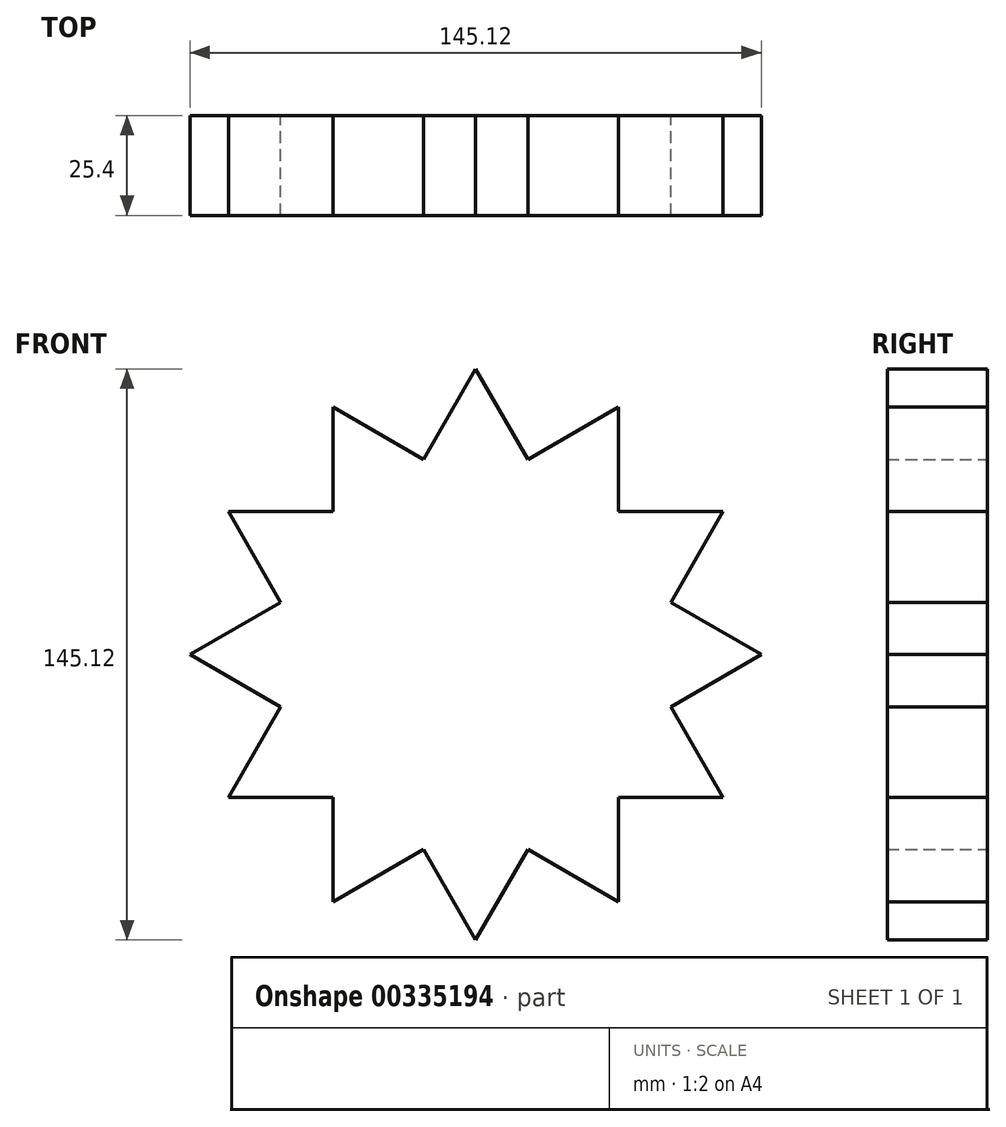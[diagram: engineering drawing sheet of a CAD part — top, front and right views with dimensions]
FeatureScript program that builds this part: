
annotation { "Feature Type Name" : "Feature", "Feature Type Description" : "" }
export const myFeature = defineFeature(function(context is Context, id is Id, definition is map)
    precondition{}
    {
        {
            var Q0;
            Q0=qCreatedBy(makeId("Front.planeOp"),FACE);
            var sketch = newSketch(context, id + "F0", { "sketchPlane" : qUnion([Q0])});
            skCircle(sketch, "E0", {"center": v(0, 0) * mm, "radius": 50.8 * mm});
            skCircle(sketch, "E1", {"center": v(0, 0) * mm, "radius": 38.1 * mm});
            skLineSegment(sketch, "E2", {"start": v(0, 72.56) * mm, "end": v(0, -70.78) * mm, "construction": true});
            skLineSegment(sketch, "E3", {"start": v(-65.47, 0) * mm, "end": v(65.57, 0) * mm, "construction": true});
            skLineSegment(sketch, "E4", {"start": v(0, 72.56) * mm, "end": v(-13.64, 48.93) * mm});
            skLineSegment(sketch, "E5.MirrorCS", {"start": v(0, 72.56) * mm, "end": v(13.64, 48.93) * mm});
            skLineSegment(sketch, "E6.anchor1", {"start": v(0, 0) * mm, "end": v(13.64, 48.93) * mm, "construction": true});
            skLineSegment(sketch, "E6.anchor2", {"start": v(0, 0) * mm, "end": v(13.64, 48.93) * mm, "construction": true});
            skLineSegment(sketch, "E7.1.0", {"start": v(-36.28, 62.84) * mm, "end": v(-12.65, 49.2) * mm});
            skLineSegment(sketch, "E7.1.1", {"start": v(-36.28, 62.84) * mm, "end": v(-36.28, 35.56) * mm});
            skLineSegment(sketch, "E7.2.0", {"start": v(-62.84, 36.28) * mm, "end": v(-35.56, 36.28) * mm});
            skLineSegment(sketch, "E7.2.1", {"start": v(-62.84, 36.28) * mm, "end": v(-49.2, 12.65) * mm});
            skLineSegment(sketch, "E7.3.0", {"start": v(-72.56, 0) * mm, "end": v(-48.93, 13.64) * mm});
            skLineSegment(sketch, "E7.3.1", {"start": v(-72.56, 0) * mm, "end": v(-48.93, -13.64) * mm});
            skLineSegment(sketch, "E7.4.0", {"start": v(-62.84, -36.28) * mm, "end": v(-49.2, -12.65) * mm});
            skLineSegment(sketch, "E7.4.1", {"start": v(-62.84, -36.28) * mm, "end": v(-35.56, -36.28) * mm});
            skLineSegment(sketch, "E7.5.0", {"start": v(-36.28, -62.84) * mm, "end": v(-36.28, -35.56) * mm});
            skLineSegment(sketch, "E7.5.1", {"start": v(-36.28, -62.84) * mm, "end": v(-12.65, -49.2) * mm});
            skLineSegment(sketch, "E7.6.0", {"start": v(0, -72.56) * mm, "end": v(-13.64, -48.93) * mm});
            skLineSegment(sketch, "E7.6.1", {"start": v(0, -72.56) * mm, "end": v(13.64, -48.93) * mm});
            skLineSegment(sketch, "E7.7.0", {"start": v(36.28, -62.84) * mm, "end": v(12.65, -49.2) * mm});
            skLineSegment(sketch, "E7.7.1", {"start": v(36.28, -62.84) * mm, "end": v(36.28, -35.56) * mm});
            skLineSegment(sketch, "E7.8.0", {"start": v(62.84, -36.28) * mm, "end": v(35.56, -36.28) * mm});
            skLineSegment(sketch, "E7.8.1", {"start": v(62.84, -36.28) * mm, "end": v(49.2, -12.65) * mm});
            skLineSegment(sketch, "E7.9.0", {"start": v(72.56, 0) * mm, "end": v(48.93, -13.64) * mm});
            skLineSegment(sketch, "E7.9.1", {"start": v(72.56, 0) * mm, "end": v(48.93, 13.64) * mm});
            skLineSegment(sketch, "E7.10.0", {"start": v(62.84, 36.28) * mm, "end": v(49.2, 12.65) * mm});
            skLineSegment(sketch, "E7.10.1", {"start": v(62.84, 36.28) * mm, "end": v(35.56, 36.28) * mm});
            skLineSegment(sketch, "E8.2.11.0", {"start": v(36.28, 62.84) * mm, "end": v(36.28, 35.56) * mm});
            skLineSegment(sketch, "E8.3.11.0", {"start": v(36.28, 62.84) * mm, "end": v(12.65, 49.2) * mm});
            skSolve(sketch);
        }
        {
            var Q0;
            Q0=qSketchRegion(id+"F0",true);
            var Q1;
            Q1=makeQuery(id+"F0.imprint","IMPRINT",FACE,{"disambiguationData":[TD([[makeQuery(id+"F0.imprint","IMPRINT",EDGE,{"derivedFrom":sQuery(id+"F0.wireOp",EDGE,"E1")}),-1.0]])]});
            var Q2;
            Q2=makeQuery(id+"F0.imprint","IMPRINT",FACE,{"disambiguationData":[TD([[makeQuery(id+"F0.imprint","IMPRINT",EDGE,{"derivedFrom":sQuery(id+"F0.wireOp",EDGE,"E1")}),1.0]])]});
            extrude(context, id + "F1", {"entities" : qUnion([Q0, Q1, Q2]), "depth" : 25.4 * mm});
        }
    });
